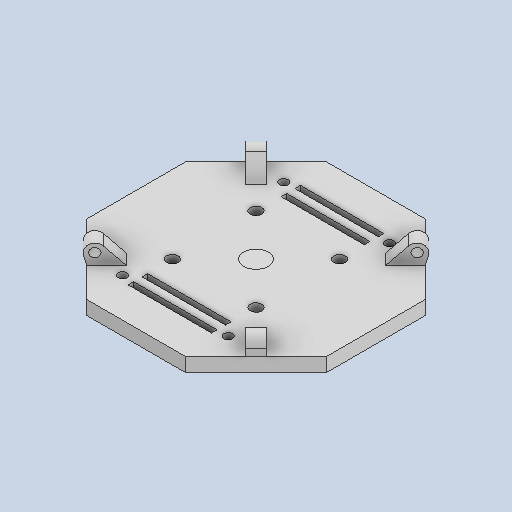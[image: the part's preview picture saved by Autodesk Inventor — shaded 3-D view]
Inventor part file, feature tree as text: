
AUTODESK INVENTOR PART (.ipt)
format: ipt  version: 2025.2 (Build 292293000, 293)  size: 210,432 bytes
history: native  units: mm
features: sketch x6, extrude x4, hole x2, plane x1, pattern_circular x1
ambient origin geometry x8: Origin, YZ Plane, XZ Plane, XY Plane, X Axis, Y Axis, Z Axis, Center Point
bodies: Solid1 (feature_tree)
feature tree (14):
  extrude  "Extrusion1"  Depth=5.0mm TaperAngle=0.0deg
  extrude  "Extrusion3"  Depth=3.0mm
  extrude  "Extrusion4"  Depth=2.0mm
  plane  "Work Plane1"
  extrude  "Extrusion5"  Depth=12.0mm
  pattern_circular  "Circular Pattern2"  [2 undecoded]
  hole  "Hole1"  [1 undecoded]
  hole  "Hole2"  [1 undecoded]
  sketch  "Sketch1"  dims[d0=86.0mm d7=5.0mm d8=0.0mm]
  sketch  "Sketch3"  dims[d21=2.0mm d22=3.0mm]
  sketch  "Sketch4"  dims[d23=2.0mm d25=15.0mm]
  sketch  "Sketch5"  dims[d27=5.0mm d28=0.0mm d30=12.0mm]
  sketch  "Sketch6"  dims[d31=0.01mm d32=0.0mm]
  sketch  "Sketch7"  dims[d33=6.0mm d34=4.0mm d35=4.0mm d36=6.0mm d37=3.2mm d38=10.0mm d39=1.0mm d40=5.5mm d41=0.0mm d42=40.0mm d43=360.0deg d45=30.1mm d46=30.1mm d52=4.2mm d53=6.0mm d54=7.0mm d55=4.0mm d56=90.0deg d57=8.0mm d58=20.594885mm d59=36.0mm d60=36.0mm d61=58.0mm d62=38.0mm d63=3.2mm d64=6.0mm d65=4.0mm d66=2.0mm d67=90.0deg d68=8.0mm d69=20.594885mm]
note: 4 required parameter values undecoded (feature->parameter linkage not recoverable at this tier; creation-order binding heuristic only, values carry confidence <= 0.55)
